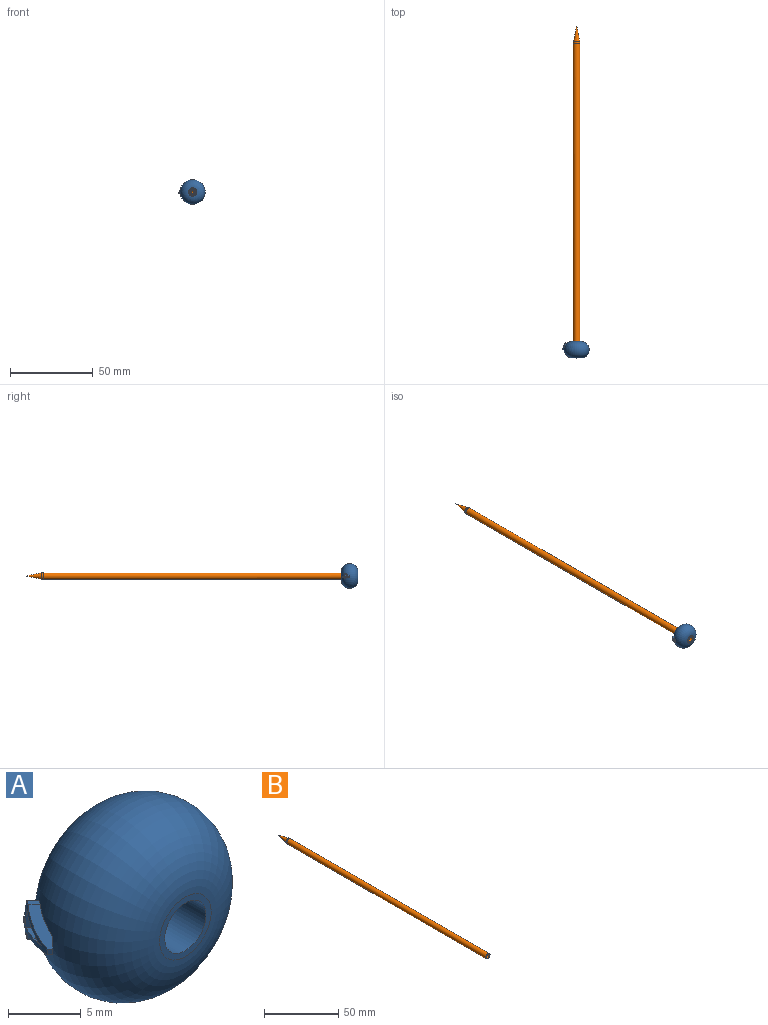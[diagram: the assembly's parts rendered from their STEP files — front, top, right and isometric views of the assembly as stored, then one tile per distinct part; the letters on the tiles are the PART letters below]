
ASSEMBLY  parts=2 mates=1
PART A: 23 faces, bbox 16.3x10.1x12.6 mm
  f0: plane 3.19x1.47mm, normal (0,0,-1), area 2.2mm2, adj f14,f15,f16,f18,f22
  f1: plane 3.1x1.88mm, normal (-0.41,-0.41,0.82), area 2.8mm2, adj f2,f15,f16,f18,f22
  f2: plane 0.94x0.81mm, normal (0,0,1), area 0.3mm2, adj f1,f3,f18,f22
  f3: plane 1.93x0.69mm, normal (0.71,0.71,0), area 1.6mm2, adj f2,f4,f18,f22
  f4: plane 1.28x1.17mm, normal (0,0,1), area 0.7mm2, adj f3,f5,f18,f22
  f5: plane 0.59x0.59mm, normal (0.71,0.71,0), area 0.3mm2, adj f4,f6,f18,f22
  f6: plane 1.29x1.17mm, normal (0,0,-1), area 0.7mm2, adj f5,f7,f18,f22
  f7: plane 0.64x0.64mm, normal (0.71,0.71,0), area 0.5mm2, adj f6,f8,f18,f22
  f8: plane 0.95x0.82mm, normal (0,0,-1), area 0.3mm2, adj f7,f14,f18,f22
  f9: extruded ~1.08x1.08mm, area 0.5mm2, adj f13,f15,f17,f18,f22
  f10: extruded ~1.57x1.57mm, area 0.8mm2, adj f11,f15,f17,f18,f22
  f11: plane 1.94x1.18mm, normal (0,0,1), area 1.1mm2, adj f10,f12,f18,f22
  f12: plane 1.48x0.65mm, normal (-0.71,-0.71,0), area 1.2mm2, adj f11,f13,f18,f22
  f13: plane 2.55x1.5mm, normal (0.41,0.41,-0.82), area 1.9mm2, adj f9,f12,f18,f22
  f14: plane 0.66x0.66mm, normal (-0.71,-0.71,0), area 0.5mm2, adj f0,f8,f18,f22
  f15: plane 1.02x0.59mm, normal (0.71,-0.71,0), area 0.6mm2, adj f0,f1,f9,f10,f16,f17,f22
  f16: plane 0.48x0.28mm, normal (-0.71,-0.71,0), area 0.2mm2, adj f0,f1,f15,f18
  f17: plane 0.56x0.56mm, normal (0.71,0.71,0), area 0mm2, adj f9,f10,f15,f18
  f18: torus R=2.5mm, axis (0,-1,0), area 4.2mm2, adj f0,f1,f2,f3,f4,f5,f6,f7
  f19: cylinder r=2mm len=10mm, axis (0,1,0), area 125.7mm2, adj f20,f21
  f20: plane 5x5mm, normal (0,-1,0), area 7.1mm2, adj f19,f22
  f21: plane 5x5mm, normal (0,1,0), area 7.1mm2, adj f19,f22
  f22: torus R=2.5mm, axis (0,-1,0), area 557.5mm2, adj f0,f1,f2,f3,f4,f5,f6,f7
PART B: 8 faces, bbox 4x200x4 mm
  f0: cylinder r=1.5mm len=190mm, axis (0,1,0), area 1790.7mm2, adj f2,f4
  f1: cylinder r=2mm len=189.51mm, axis (0,1,0), area 2381.4mm2, adj f2,f5
  f2: plane 4x4mm, normal (0,-1,0), area 5.5mm2, adj f0,f1
  f3: cone r=2mm half-angle=11.3deg, axis (0,-1,0), area 58mm2, adj f5
  f4: plane 3x3mm, normal (0,-1,0), area 4.1mm2, adj f0,f6
  f5: revolved ~4x4mm, area 12.2mm2, adj f1,f3
  f6: revolved ~1.94x1.94mm, area 1.7mm2, adj f4,f7
  f7: cone r=1.02mm half-angle=11.3deg, axis (0,-1,0), area 13.6mm2, adj f6
PLACE A t=(8.96,13.65,5.71)mm fixed
PLACE B t=(8.96,193.65,5.71)mm
MATE fastened B.f0 <-> A.f19  axis (0,-1,0) through (8.96,3.65,5.71)mm
